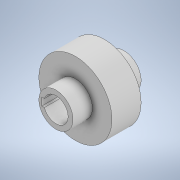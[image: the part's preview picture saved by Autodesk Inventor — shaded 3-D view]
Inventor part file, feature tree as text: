
AUTODESK INVENTOR PART (.ipt)
format: ipt  version: 2020 (Build 240168000, 168)  size: 137,728 bytes
history: native  units: in
note: dims shown in document units (in); Inventor stores cm internally (conversion verified against a paired STEP export)
features: sketch x5, extrude x4
ambient origin geometry x8: Origin, YZ Plane, XZ Plane, XY Plane, X Axis, Y Axis, Z Axis, Center Point
bodies: Solid1 (feature_tree)
feature tree (9):
  extrude  "Extrusion1"  Depth=1.1811in TaperAngle=0.0deg
  extrude  "Extrusion2"  Depth=1.378in
  extrude  "Extrusion3"  Depth=0.1575in
  extrude  "Extrusion4"  Depth=0.7874in TaperAngle=0.0deg
  sketch  "Sketch5"  dims[d11=0.315in d12=0.7874in d13=0.0in]
  sketch  "Sketch1"  dims[d0=2.9528in d1=1.1811in d2=0.0in]
  sketch  "Sketch2"  dims[d3=1.378in d4=0.9843in]
  sketch  "Sketch3"  dims[d5=0.7874in d6=0.0in d7=0.1575in]
  sketch  "Sketch4"  dims[d8=0.315in d9=0.7874in d10=0.0in]
